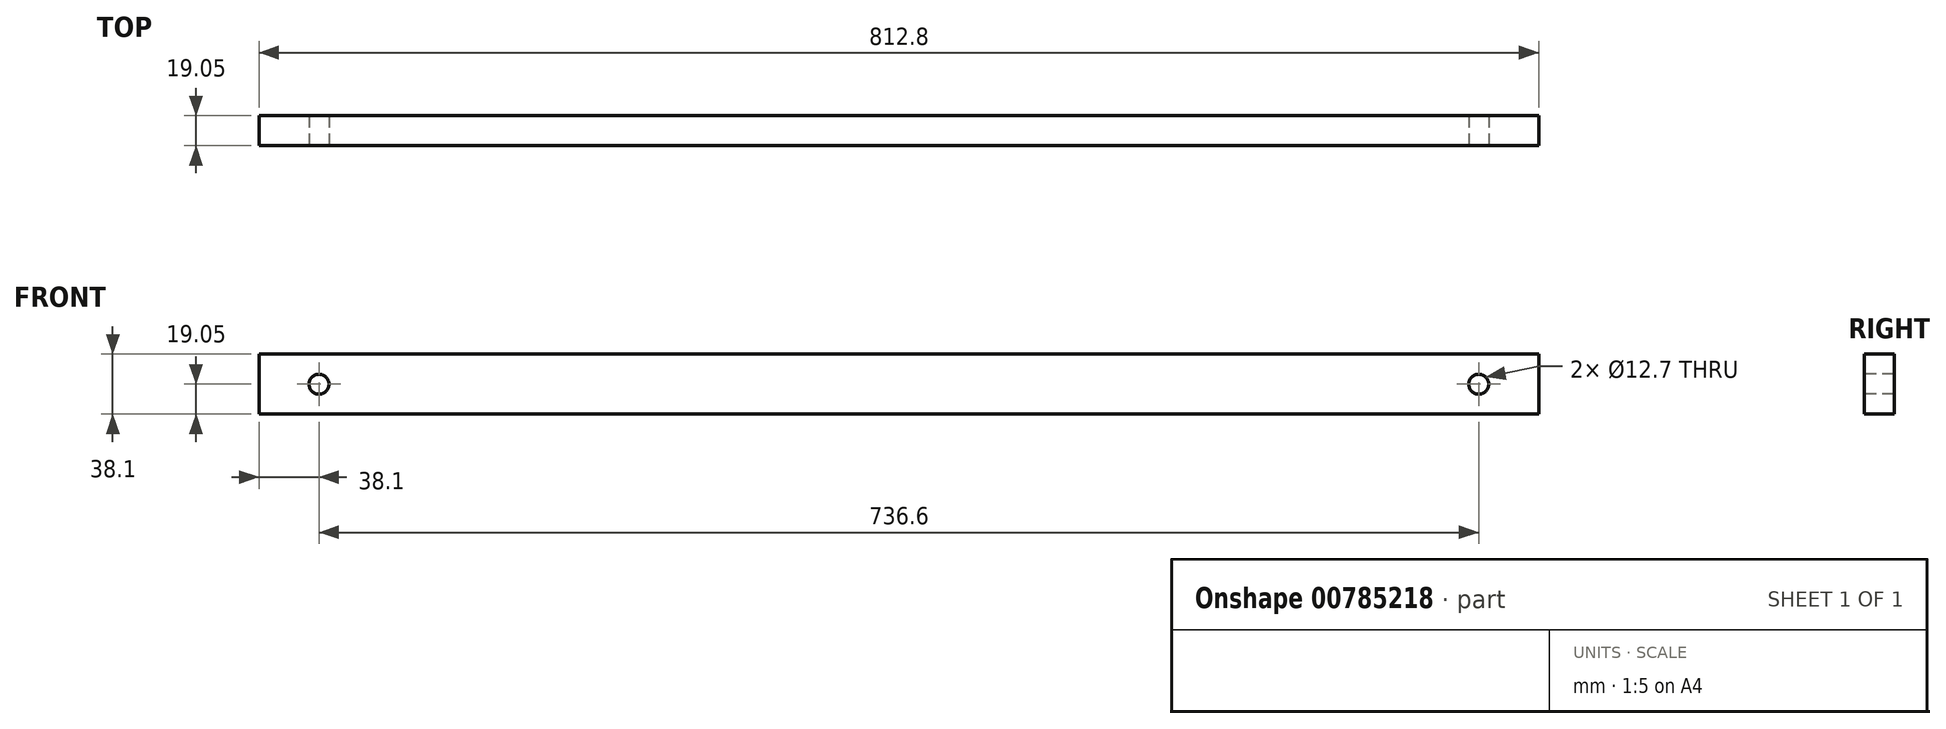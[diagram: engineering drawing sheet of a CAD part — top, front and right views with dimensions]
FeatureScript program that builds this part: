
annotation { "Feature Type Name" : "Feature", "Feature Type Description" : "" }
export const myFeature = defineFeature(function(context is Context, id is Id, definition is map)
    precondition{}
    {
        {
            var Q0;
            Q0=qCreatedBy(makeId("Front.planeOp"),FACE);
            var sketch = newSketch(context, id + "F0", { "sketchPlane" : qUnion([Q0])});
            skLineSegment(sketch, "E0.bottom", {"start": v(-280.1, 53.57) * mm, "end": v(532.7, 53.57) * mm});
            skLineSegment(sketch, "E0.top", {"start": v(-280.1, 15.47) * mm, "end": v(532.7, 15.47) * mm});
            skLineSegment(sketch, "E0.right", {"start": v(532.7, 53.57) * mm, "end": v(532.7, 15.47) * mm});
            skLineSegment(sketch, "E1", {"start": v(-280.1, 53.57) * mm, "end": v(-280.1, 15.47) * mm});
            skSolve(sketch);
        }
        {
            var Q0;
            Q0=makeQuery(id+"F0.imprint","IMPRINT",FACE,{"disambiguationData":[TD([[makeQuery(id+"F0.imprint","IMPRINT",EDGE,{"derivedFrom":sQuery(id+"F0.wireOp",EDGE,"E0.bottom")}),-1.0]])]});
            extrude(context, id + "F1", {"entities" : qUnion([Q0]), "depth" : 19.05 * mm, "offsetDistance" : 25.4 * mm});
        }
        {
            var Q0;
            Q0=makeQuery(id+"F1.opExtrude","CAP_FACE",FACE,{"disambiguationData":[OSD([sQuery(id+"F0.wireOp",EDGE,"E0.bottom"),sQuery(id+"F0.wireOp",EDGE,"E0.top"),sQuery(id+"F0.wireOp",EDGE,"E0.left"),sQuery(id+"F0.wireOp",EDGE,"E0.right")])],"isStart":false});
            var sketch = newSketch(context, id + "F2", { "sketchPlane" : qUnion([Q0])});
            skCircle(sketch, "E2", {"center": v(-242, 34.52) * mm, "radius": 6.35 * mm});
            skSolve(sketch);
        }
        {
            var Q0;
            Q0=makeQuery(id+"F2.imprint","IMPRINT",FACE,{"disambiguationData":[TD([[makeQuery(id+"F2.imprint","IMPRINT",EDGE,{"derivedFrom":sQuery(id+"F2.wireOp",EDGE,"E2")}),1.0]])]});
            extrude(context, id + "F3", {"entities" : qUnion([Q0]), "operationType" : NewBodyOperationType.REMOVE, "endBound" : BoundingType.THROUGH_ALL, "oppositeDirection" : true, "depth" : 25.4 * mm, "offsetDistance" : 25.4 * mm});
        }
        {
            var Q0;
            Q0=makeQuery(id+"F1.opExtrude","CAP_FACE",FACE,{"disambiguationData":[OSD([sQuery(id+"F0.wireOp",EDGE,"E0.bottom"),sQuery(id+"F0.wireOp",EDGE,"E0.top"),sQuery(id+"F0.wireOp",EDGE,"E0.right"),sQuery(id+"F0.wireOp",EDGE,"E1")])],"isStart":false});
            var sketch = newSketch(context, id + "F4", { "sketchPlane" : qUnion([Q0])});
            skCircle(sketch, "E3", {"center": v(494.6, 34.52) * mm, "radius": 6.35 * mm});
            skSolve(sketch);
        }
        {
            var Q0;
            Q0 = qSketchRegion(id + "F4", true);
            extrude(context, id + "F5", {"entities" : qUnion([Q0]), "operationType" : NewBodyOperationType.REMOVE, "endBound" : BoundingType.THROUGH_ALL, "oppositeDirection" : true, "depth" : 25.4 * mm, "offsetDistance" : 25.4 * mm});
        }
    });
